MODEL slx_335626045161
CONFIG AbsTol = auto
CONFIG FixedStep = 0.01
CONFIG MaxStep = auto
CONFIG MinStep = auto
CONFIG RelTol = 1e-3
CONFIG SampleTimeConstraint = Unconstrained
CONFIG Solver = FixedStepDiscrete
CONFIG SolverMode = Auto
CONFIG SolverName = FixedStepDiscrete
CONFIG StartTime = 0.0
CONFIG StopTime = 10.0
BLOCK [Constant] Constant
BLOCK [Constant] Constant1
  Value = 5
BLOCK [Constant] Constant2
  Value = -1
BLOCK [Mux] Mux
  DisplayOption = bar
  Inputs = 2
  Ports = [2, 1]
BLOCK [Reference] Ramp  REF=simulink/Sources/Ramp
  Ports = [0, 1]
  SourceBlock = simulink/Sources/Ramp
  SourceType = Ramp
BLOCK [RelationalOperator] Relational Operator
  InputSameDT = off
  Operator = >
  OutDataTypeStr = boolean
  Ports = [2, 1]
BLOCK [Scope] Scope
  Ports = [1]
  ScopeSpecificationString = Simulink.scopes.TimeScopeBlockCfg('CurrentConfiguration', extmgr.ConfigurationSet(extmgr.Configuration('Core','General UI',true),extmgr.Configuration('Core','Source UI',true),extmgr.Configuration('Sources','WiredSimulink',true),extmgr.Configuration('Visuals','Time Domain',true,'SerializedDisplays',{struct('MinYLimReal','-2.375','MaxYLimReal','11.375','YLabelReal','','MinYLimMag','0.00000','MaxYLim...<+1355ch>
BLOCK [Switch] Switch
  Criteria = u2 ~= 0
  InputSameDT = off
  SaturateOnIntegerOverflow = off
LINE Constant1:1 -> Relational Operator:2
LINE Constant2:1 -> Switch:3
LINE Constant:1 -> Switch:1
LINE Mux:1 -> Scope:1
LINE Ramp:1 -> Mux:1
LINE Ramp:1 -> Relational Operator:1
LINE Relational Operator:1 -> Switch:2
LINE Switch:1 -> Mux:2
